# Revit family: MADEL_GRILL_AIR RETURN_FIXED BLADES 45º_DMT+(PLRX - PLRXL) – (2.D1)
name_source: partatom
category: Terminales de aire
revit_build: Autodesk Revit 2015 (Build: 20140606_1530(x64)
units: mm (PartAtom-declared; Revit-internal decimal feet)

## types (1)
- MADEL_GRILL_AIR RETURN_FIXED BLADES 45º_DMT+(PLRX - PLRXL) – (2.D1)
    Afree = 0.1250 m²
    B = 730 mm  [stored 2.39501 ft]
    BIMETRICAL = http://www.bimetrical.com
    BIMETRICAL Category = AirTerminal
    Blade Lenght = 685 mm  [stored 2.24738 ft]
    Comentarios de tipo = The DMT series grilles are designed to be used in extractors of cold and hot air. They are mounted on walls or in false ceilings.
    D1 = 248 mm
    D_Connector = 250 mm  [stored 0.82021 ft]
    Descripción = MADEL_Fixed blades air return grilles
    E = 320 mm  [stored 1.04987 ft]
    Fabricante = MADEL
    Family Version = 1.0
    Flujo máx. = 1,350 m³/h
    Flujo mín. = 675 m³/h
    H = 300 mm
    H1 = 285 mm  [stored 0.935039 ft]
    H2 = 31.7 mm
    IfcExportAs = IfcAirTerminalType
    IfcExportType = IfcAirTerminalType
    Imagen de tipo = <Ninguno>
    Kf = 1.617787
    L = 700 mm  [stored 2.29659 ft]
    L3 = 685 mm  [stored 2.24738 ft]
    Material Grill = MADEL_M9016
    Material Plenum Box = <Por categoría>
    Modelo = DMT-AR+PLRX/L 700x300
    N_Graphic lines = 8
    Nº  Blades = 11
    Nº Plenum Connections = 2
    PLRX = No
    PLRX/L = Sí
    Plenum Connection Type = Lateral
    Product Size = 700x300
    Review Date = 11/2016
    Revit Version = Revit 2015 - English
    URL = http://www.madel.com
    Vmax = 3.0 m/s
    Vmed = 2.3 m/s
    Vmin = 1.5 m/s
    b_factor = -0.128138
    m_factor = 1.899495

note: [stored X ft] marks values corroborated as IEEE doubles in the binary element streams (Revit-internal decimal feet)

## geometry (parser evidence)
native form markers: Blend x4
no freeform markers — native parametric forms only
